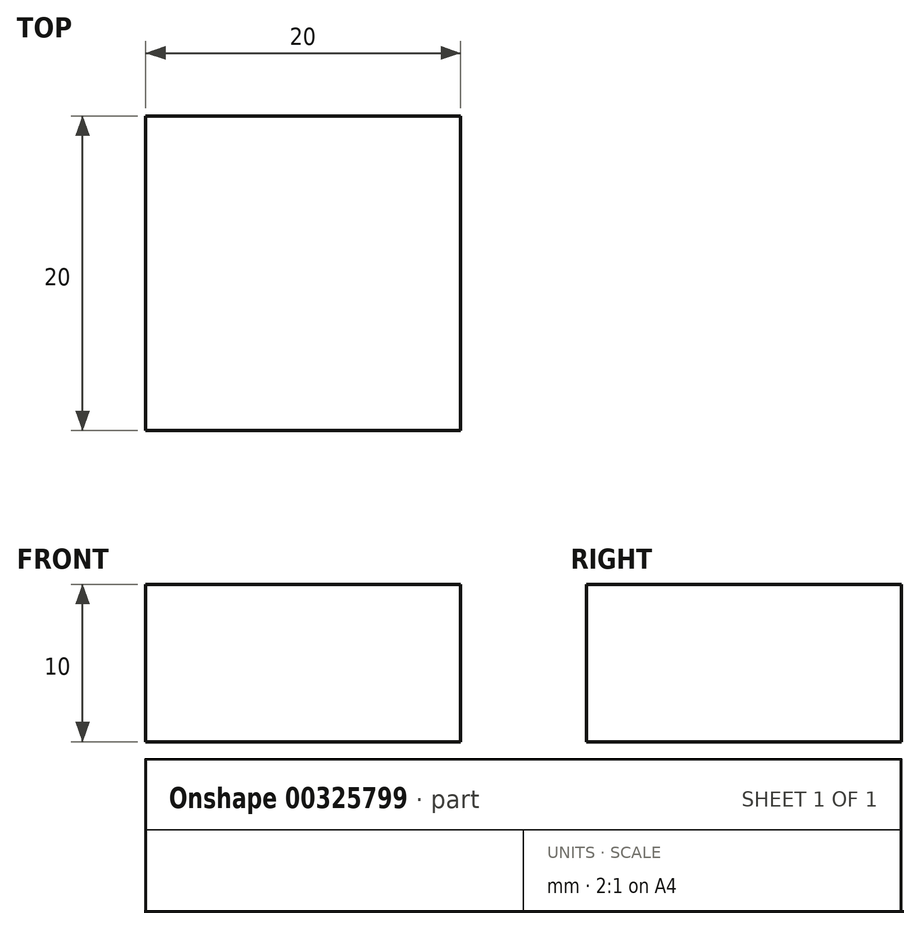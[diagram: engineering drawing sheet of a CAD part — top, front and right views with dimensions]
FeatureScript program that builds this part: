
annotation { "Feature Type Name" : "Feature", "Feature Type Description" : "" }
export const myFeature = defineFeature(function(context is Context, id is Id, definition is map)
    precondition{}
    {
        {
            var Q0;
            Q0=qCreatedBy(makeId("Top.planeOp"),FACE);
            var sketch = newSketch(context, id + "F0", { "sketchPlane" : qUnion([Q0])});
            skLineSegment(sketch, "E0.bottom", {"start": v(10, -10) * mm, "end": v(-10, -10) * mm});
            skLineSegment(sketch, "E0.top", {"start": v(10, 10) * mm, "end": v(-10, 10) * mm});
            skLineSegment(sketch, "E0.left", {"start": v(10, -10) * mm, "end": v(10, 10) * mm});
            skLineSegment(sketch, "E0.right", {"start": v(-10, -10) * mm, "end": v(-10, 10) * mm});
            skPoint(sketch, "E0.middle", {"position": v(0, 0) * mm});
            skSolve(sketch);
        }
        {
            var Q0;
            Q0 = qSketchRegion(id + "F0", true);
            extrude(context, id + "F1", {"entities" : qUnion([Q0]), "depth" : 10 * mm});
        }
    });
